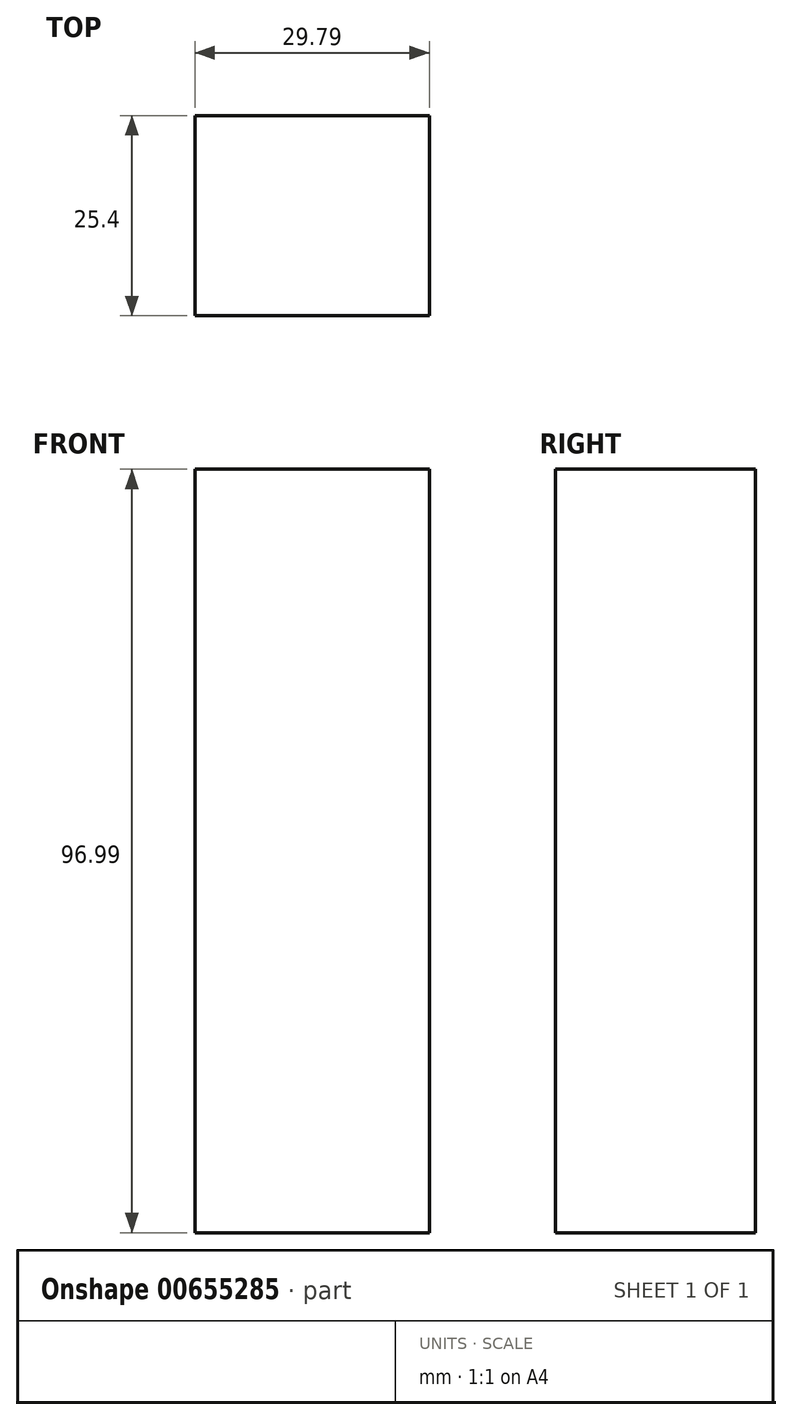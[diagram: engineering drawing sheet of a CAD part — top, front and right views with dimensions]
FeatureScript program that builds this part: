
annotation { "Feature Type Name" : "Feature", "Feature Type Description" : "" }
export const myFeature = defineFeature(function(context is Context, id is Id, definition is map)
    precondition{}
    {
        {
            var Q0;
            Q0=qCreatedBy(makeId("Front.planeOp"),FACE);
            var sketch = newSketch(context, id + "F0", { "sketchPlane" : qUnion([Q0])});
            skLineSegment(sketch, "E0", {"start": v(0, 0) * mm, "end": v(0, 54.83) * mm});
            skLineSegment(sketch, "E1", {"start": v(0, 54.83) * mm, "end": v(-29.79, 54.83) * mm});
            skLineSegment(sketch, "E2", {"start": v(-29.79, 54.83) * mm, "end": v(-29.79, -42.16) * mm});
            skLineSegment(sketch, "E3", {"start": v(-29.79, -42.16) * mm, "end": v(0, -42.16) * mm});
            skLineSegment(sketch, "E4", {"start": v(0, -42.16) * mm, "end": v(0, 0) * mm});
            skSolve(sketch);
        }
        {
            var Q0;
            Q0=makeQuery(id+"F0.imprint","IMPRINT",FACE,{"disambiguationData":[TD([[makeQuery(id+"F0.imprint","IMPRINT",EDGE,{"derivedFrom":sQuery(id+"F0.wireOp",EDGE,"E0")}),1.0]])]});
            extrude(context, id + "F1", {"entities" : qUnion([Q0]), "depth" : 25.4 * mm, "offsetDistance" : 25.4 * mm});
        }
    });
